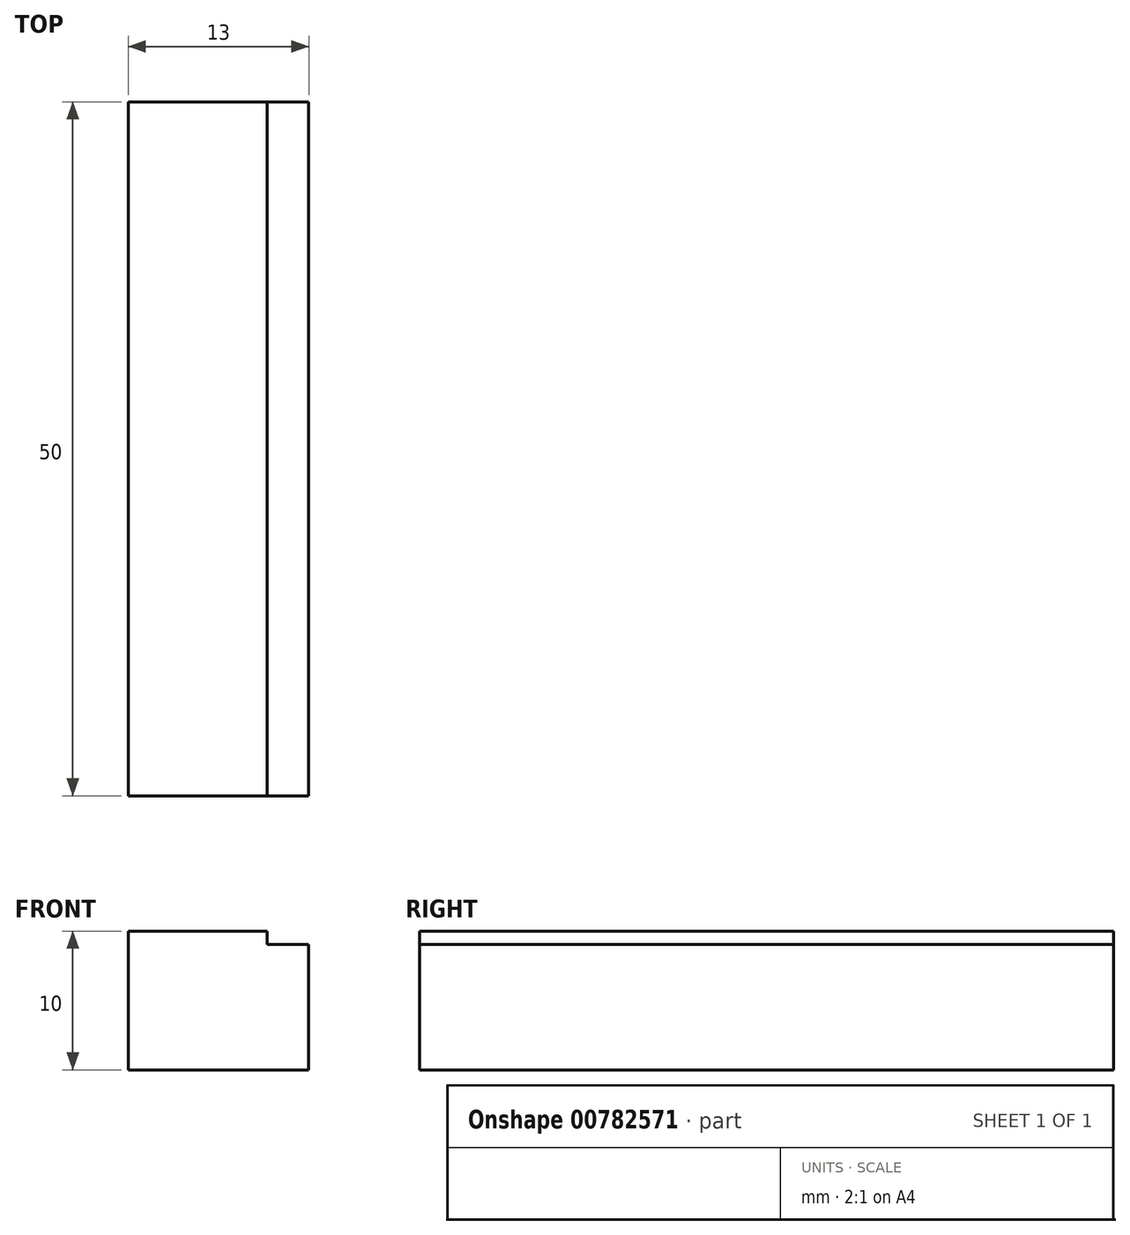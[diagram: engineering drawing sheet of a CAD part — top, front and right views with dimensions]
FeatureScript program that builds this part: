
annotation { "Feature Type Name" : "Feature", "Feature Type Description" : "" }
export const myFeature = defineFeature(function(context is Context, id is Id, definition is map)
    precondition{}
    {
        {
            var Q0;
            Q0=qCreatedBy(makeId("Top.planeOp"),FACE);
            var sketch = newSketch(context, id + "F0", { "sketchPlane" : qUnion([Q0])});
            skLineSegment(sketch, "E0.bottom", {"start": v(-61.91, 12.34) * mm, "end": v(-71.91, 12.34) * mm});
            skLineSegment(sketch, "E0.top", {"start": v(-61.91, 62.34) * mm, "end": v(-71.91, 62.34) * mm});
            skLineSegment(sketch, "E0.left", {"start": v(-61.91, 12.34) * mm, "end": v(-61.91, 62.34) * mm});
            skLineSegment(sketch, "E0.right", {"start": v(-71.91, 12.34) * mm, "end": v(-71.91, 62.34) * mm});
            skPoint(sketch, "E0.middle", {"position": v(-66.91, 37.34) * mm});
            skSolve(sketch);
        }
        {
            var Q0;
            Q0=makeQuery(id+"F0.imprint","IMPRINT",FACE,{"disambiguationData":[TD([[makeQuery(id+"F0.imprint","IMPRINT",EDGE,{"derivedFrom":sQuery(id+"F0.wireOp",EDGE,"E0.bottom")}),-1.0]])]});
            extrude(context, id + "F1", {"entities" : qUnion([Q0]), "depth" : 10 * mm, "offsetDistance" : 25 * mm});
        }
        {
            var Q0;
            Q0=makeQuery(id+"F1.opExtrude","SWEPT_FACE",FACE,{"disambiguationData":[OSD([sQuery(id+"F0.wireOp",EDGE,"E0.left")])]});
            var sketch = newSketch(context, id + "F2", { "sketchPlane" : qUnion([Q0])});
            skLineSegment(sketch, "E1.bottom", {"start": v(62.34, 0) * mm, "end": v(12.34, 0) * mm});
            skLineSegment(sketch, "E1.top", {"start": v(62.34, 9.03) * mm, "end": v(12.34, 9.03) * mm});
            skLineSegment(sketch, "E1.left", {"start": v(62.34, 0) * mm, "end": v(62.34, 9.03) * mm});
            skLineSegment(sketch, "E1.right", {"start": v(12.34, 0) * mm, "end": v(12.34, 9.03) * mm});
            skPoint(sketch, "E1.middle", {"position": v(37.34, 4.52) * mm});
            skPoint(sketch, "E1.middle.positionSnap0", {"position": v(37.34, 0) * mm});
            skPoint(sketch, "E1.centerSnap0", {"position": v(37.34, 0) * mm});
            skSolve(sketch);
        }
        {
            var Q0;
            Q0 = qSketchRegion(id + "F2", true);
            extrude(context, id + "F3", {"entities" : qUnion([Q0]), "operationType" : NewBodyOperationType.ADD, "depth" : 3 * mm, "offsetDistance" : 25 * mm});
        }
    });
